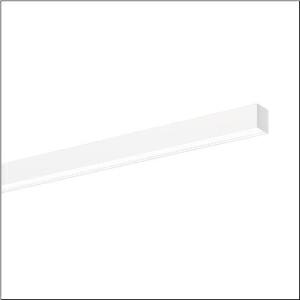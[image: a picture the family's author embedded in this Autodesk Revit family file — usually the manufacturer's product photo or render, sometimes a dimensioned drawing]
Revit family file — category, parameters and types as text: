
# Revit family: silica_r__21_51mx23dc3awb_8ef9
name_source: partatom
category: Lighting Fixtures
units: mm (PartAtom-declared; Revit-internal decimal feet)

## family parameters
Cut with Voids When Loaded = No
Host = Face
Light Source = No
Part Type = Normal
Room Calculation Point = No
Round Connector Dimension = Use Diameter
Shared = No

## types (1)
- --- (1 x LED, 8200 lm, 62.2 W, 3000K)
    Apparent Load = 62 VA
    CIE Flux Codes = 78 96 99 100 100
    Color Rendering = 80
    Color Temperature = 3000K
    Default Elevation = 1800 mm
    Description = Silica® 21, office luminaire, primary optical cover: prismatic diffuser, of PMMA, CAT 2 (L<= 3000cd/m²), light emission: direct distribution, primary light characteristic: symmetric, installation type: surface-mounted, LED, rated luminous flux: 8.200lm, luminous efficacy: 132lm/W, light colour: 830, colour temperature: 3000K, with terminal, 3+2-pole, max. 2.5mm², mains connection: 220..240V, AC, 50/60Hz, rated input power: 62.2W, luminaire housing, of aluminium, traffic white (RAL 9016), length: 3.004mm, width: 53mm, height: 53mm, protection rating (complete): IP20, insulation class (complete): insulation class I (protective earthing), certification: CE, permissible operating ambient temperature: 0..+35°C, standard: EN 50419, packaging unit: 1 piece
    Height = 0 mm  [stored 0 ft]
    Lamp = 1 x LED
    Lamp Light Flux = 8200 lm
    Lamp Power = 62.2 W
    Lamp count = 1
    Length = 3004 mm
    Luminous efficacy = 132 lm/W
    Manufacturer = Siteco
    ModVariant = No
    Model = 51MX23DC3AWB
    Mounting Place = Ceiling
    Mounting Type = Recessed
    Number of Poles = 1
    OnlyDefault = Yes
    Power Factor = 1
    Product Name = Silica® 21
    Product group = office luminaire | ceiling recessed
    ProductGroupID = 401
    Protection Class = Protection class I
    Protection Degree = IP 20
    RLX_Detail_Level = 1
    RLX_Emergency_Light_Flux = 0 lm
    RLX_Emergency_Type = 0
    RLX_Emergency_Type_DB = No
    RlxData = <blob elided: 18693 chars, md5=1a5ea621>
    Socket = socket
    Standby Power = 0 W
    System Light Flux = 8200 lm
    System Power = 62 W
    Type Comments = factory setting: luminous flux: 100 % | dim-lin: 254 | 345 mA
    Type Image = l_1297777.jpg
    URL = http://relux.com
    VarID = @adj_050075
    Voltage = 0 V
    Weight = 0.00 kg
    Width = 53 mm

note: [stored X ft] marks values corroborated as IEEE doubles in the binary element streams (Revit-internal decimal feet)

## geometry (parser evidence)
native form markers: Blend x4, Sweep x11
no freeform markers — native parametric forms only
